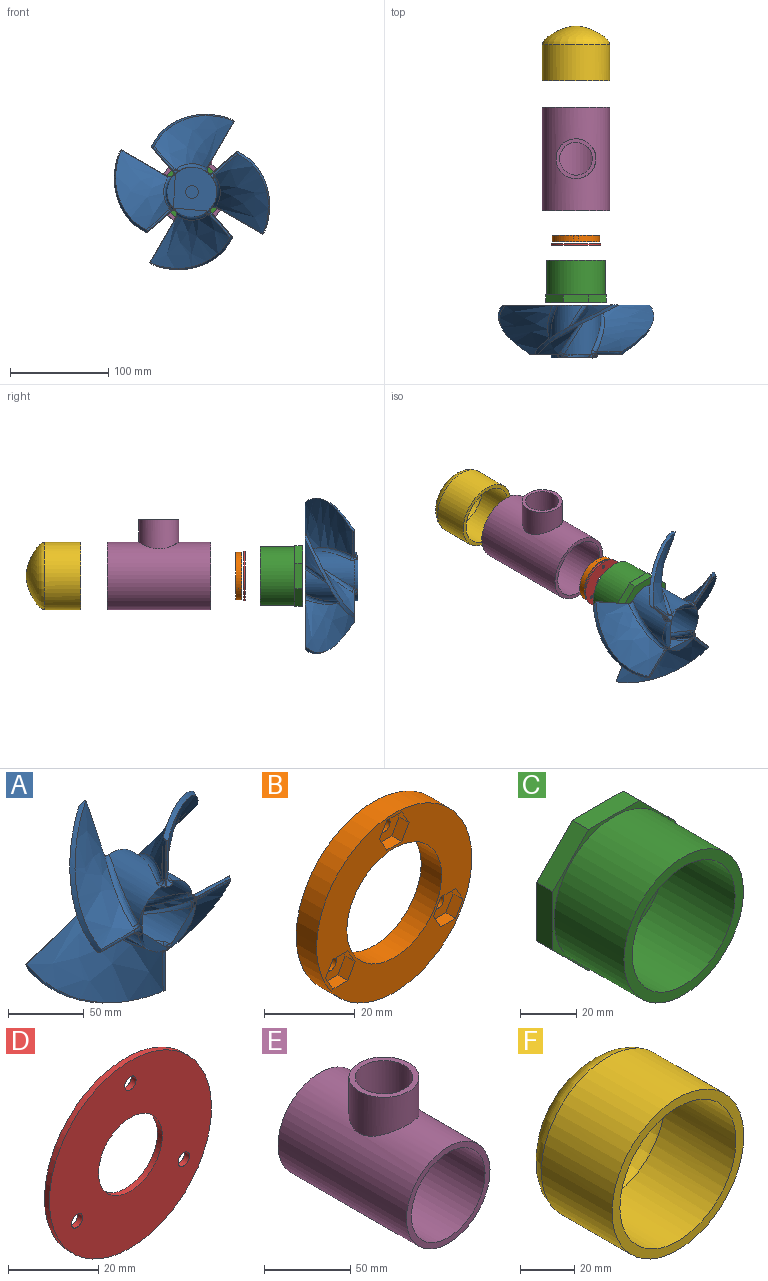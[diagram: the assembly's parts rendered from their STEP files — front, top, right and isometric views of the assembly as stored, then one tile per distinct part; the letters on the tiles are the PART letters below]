
ASSEMBLY  parts=6 mates=5
PART A: 68 faces, bbox 182.4x97.7x182.4 mm
  f0: cylinder r=25.4mm len=50.14mm, axis (0,1,0), area 1388.4mm2, adj f28,f41,f42,f43,f65
  f1: cylinder r=25.4mm len=50.14mm, axis (0,1,0), area 1388.4mm2, adj f28,f48,f49,f50,f65
  f2: cylinder r=25.4mm len=50.14mm, axis (0,1,0), area 1388.4mm2, adj f28,f29,f55,f56,f65
  f3: bspline ~88.12x82.83mm, area 3439.5mm2, adj f8,f34,f60,f65
  f4: plane 32.17x1.13mm, normal (0,-0.85,0.53), area 14.9mm2, adj f7,f8,f32,f60
  f5: bspline ~85.79x85.35mm, area 3695.9mm2, adj f6,f7,f29,f30,f60,f64
  f6: plane 51.13x17.15mm, normal (-0.51,0.85,-0.16), area 35.2mm2, adj f5,f60,f64,f65
  f7: bspline ~31.48x2.18mm, area 62.3mm2, adj f4,f5,f31,f60
  f8: bspline ~68.56x3.02mm, area 87mm2, adj f3,f4,f33,f35,f60
  f9: bspline ~88.12x82.83mm, area 3439.5mm2, adj f14,f41,f59,f65
  f10: plane 32.17x1.13mm, normal (-0.53,-0.85,0), area 14.9mm2, adj f13,f14,f39,f59
  f11: bspline ~85.79x85.35mm, area 3695.9mm2, adj f12,f13,f36,f37,f59,f63
  f12: plane 51.13x17.15mm, normal (0.16,0.85,-0.51), area 35.2mm2, adj f11,f59,f63,f65
  f13: bspline ~31.48x2.18mm, area 62.3mm2, adj f10,f11,f38,f59
  f14: bspline ~68.56x3.02mm, area 87mm2, adj f9,f10,f40,f42,f59
  f15: bspline ~88.12x82.83mm, area 3439.5mm2, adj f20,f48,f58,f65
  f16: plane 32.17x1.13mm, normal (0,-0.85,-0.53), area 14.9mm2, adj f19,f20,f46,f58
  f17: bspline ~85.79x85.35mm, area 3695.9mm2, adj f18,f19,f43,f44,f58,f62
  f18: plane 51.13x17.15mm, normal (0.51,0.85,0.16), area 35.2mm2, adj f17,f58,f62,f65
  f19: bspline ~31.48x2.18mm, area 62.3mm2, adj f16,f17,f45,f58
  f20: bspline ~68.56x3.02mm, area 87mm2, adj f15,f16,f47,f49,f58
  f21: bspline ~88.12x82.83mm, area 3439.5mm2, adj f26,f55,f57,f65
  f22: plane 32.17x1.13mm, normal (0.53,-0.85,0), area 14.9mm2, adj f25,f26,f53,f57
  f23: bspline ~85.79x85.35mm, area 3695.9mm2, adj f24,f25,f50,f51,f57,f61
  f24: plane 51.13x17.15mm, normal (-0.16,0.85,0.51), area 35.2mm2, adj f23,f57,f61,f65
  f25: bspline ~31.48x2.18mm, area 62.3mm2, adj f22,f23,f52,f57
  f26: bspline ~68.56x3.02mm, area 87mm2, adj f21,f22,f54,f56,f57
  f27: cylinder r=25.4mm len=50.14mm, axis (0,1,0), area 1388.4mm2, adj f28,f34,f35,f36,f65
  f28: revolved ~50.8x50.8mm, area 5109.2mm2, adj f0,f1,f2,f27,f29,f30,f31,f32
  f29: bspline ~54.51x27.12mm, area 320.1mm2, adj f2,f5,f28,f30,f64,f65
  f30: bspline ~5.63x4.85mm, area 11.6mm2, adj f5,f28,f29,f31
  f31: bspline ~6.43x4.12mm, area 21.8mm2, adj f7,f28,f30,f32
  f32: bspline ~7.96x6.87mm, area 3.1mm2, adj f4,f28,f31,f33
  f33: bspline ~4.1x3.79mm, area 9.6mm2, adj f8,f28,f32,f35
  f34: bspline ~53.78x31.69mm, area 305.8mm2, adj f3,f27,f35,f65
  f35: bspline ~5.55x3.78mm, area 14.8mm2, adj f8,f27,f28,f33,f34
  f36: bspline ~54.51x27.12mm, area 320.1mm2, adj f11,f27,f28,f37,f63,f65
  f37: bspline ~5.63x4.85mm, area 11.6mm2, adj f11,f28,f36,f38
  f38: bspline ~6.43x4.12mm, area 21.8mm2, adj f13,f28,f37,f39
  f39: bspline ~7.96x6.87mm, area 3.1mm2, adj f10,f28,f38,f40
  f40: bspline ~4.1x3.79mm, area 9.6mm2, adj f14,f28,f39,f42
  f41: bspline ~53.78x31.69mm, area 305.8mm2, adj f0,f9,f42,f65
  f42: bspline ~5.55x3.78mm, area 14.8mm2, adj f0,f14,f28,f40,f41
  f43: bspline ~54.51x27.12mm, area 320.1mm2, adj f0,f17,f28,f44,f62,f65
  f44: bspline ~5.63x4.85mm, area 11.6mm2, adj f17,f28,f43,f45
  f45: bspline ~6.43x4.12mm, area 21.8mm2, adj f19,f28,f44,f46
  f46: bspline ~3.79x3.17mm, area 3.1mm2, adj f16,f28,f45,f47
  f47: bspline ~4.1x3.79mm, area 9.6mm2, adj f20,f28,f46,f49
  f48: bspline ~53.78x31.69mm, area 305.8mm2, adj f1,f15,f49,f65
  f49: bspline ~5.55x3.78mm, area 14.8mm2, adj f1,f20,f28,f47,f48
  f50: bspline ~54.51x27.12mm, area 320.1mm2, adj f1,f23,f28,f51,f61,f65
  f51: bspline ~5.63x4.85mm, area 11.6mm2, adj f23,f28,f50,f52
  f52: bspline ~6.43x4.12mm, area 21.8mm2, adj f25,f28,f51,f53
  f53: bspline ~3.79x3.17mm, area 3.1mm2, adj f22,f28,f52,f54
  f54: bspline ~4.1x3.79mm, area 9.6mm2, adj f26,f28,f53,f56
  f55: bspline ~53.78x31.69mm, area 305.8mm2, adj f2,f21,f56,f65
  f56: bspline ~5.55x3.78mm, area 14.8mm2, adj f2,f26,f28,f54,f55
  f57: revolved ~80.25x66.46mm, area 381.9mm2, adj f21,f22,f23,f24,f25,f26,f65
  f58: revolved ~80.25x66.46mm, area 381.9mm2, adj f15,f16,f17,f18,f19,f20,f65
  f59: revolved ~80.25x66.46mm, area 381.9mm2, adj f9,f10,f11,f12,f13,f14,f65
  f60: revolved ~80.25x66.46mm, area 381.9mm2, adj f3,f4,f5,f6,f7,f8,f65
  f61: bspline ~2.2x1.56mm, area 0.6mm2, adj f23,f24,f50,f65
  f62: bspline ~2.2x1.56mm, area 0.6mm2, adj f17,f18,f43,f65
  f63: bspline ~2.2x1.56mm, area 0.6mm2, adj f11,f12,f36,f65
  f64: bspline ~2.2x1.56mm, area 0.6mm2, adj f5,f6,f29,f65
  f65: plane 161.14x161.14mm, normal (0,1,0), area 3088.6mm2, adj f0,f1,f2,f3,f6,f9,f12,f15
  f66: plane 12.7x12.7mm, normal (0,1,0), area 126.7mm2, adj f67
  f67: cylinder r=6.35mm len=24.74mm, axis (0,1,0), area 986.9mm2, adj f65,f66
PART B: 28 faces, bbox 48.3x6.4x48.3 mm
  f0: plane 48.26x48.26mm, normal (0,-1,0), area 981.1mm2, adj f1,f2,f4,f5,f6,f7,f8,f9
  f1: cylinder r=14.73mm len=29.46mm, axis (0,1,0), area 587.8mm2, adj f0,f3
  f2: cylinder r=24.13mm len=48.26mm, axis (0,1,0), area 962.7mm2, adj f0,f3
  f3: plane 48.26x48.26mm, normal (0,1,0), area 1117.6mm2, adj f1,f2,f25,f26,f27
  f4: plane 4.62x3.05mm, normal (0,0,1), area 14.1mm2, adj f0,f5,f9,f10
  f5: plane 4x3.05mm, normal (-0.87,0,0.5), area 14.1mm2, adj f0,f4,f6,f10
  f6: plane 4x3.05mm, normal (-0.87,0,-0.5), area 14.1mm2, adj f0,f5,f7,f10
  f7: plane 4.62x3.05mm, normal (0,0,-1), area 14.1mm2, adj f0,f6,f8,f10
  f8: plane 4x3.05mm, normal (0.87,0,-0.5), area 14.1mm2, adj f0,f7,f9,f10
  f9: plane 4x3.05mm, normal (0.87,0,0.5), area 14.1mm2, adj f0,f4,f8,f10
  f10: plane 9.24x8mm, normal (0,-1,0), area 45.5mm2, adj f4,f5,f6,f7,f8,f9,f27
  f11: plane 4x3.05mm, normal (0.87,0,-0.5), area 14.1mm2, adj f0,f12,f16,f17
  f12: plane 4x3.05mm, normal (0.87,0,0.5), area 14.1mm2, adj f0,f11,f13,f17
  f13: plane 4.62x3.05mm, normal (0,0,1), area 14.1mm2, adj f0,f12,f14,f17
  f14: plane 4x3.05mm, normal (-0.87,0,0.5), area 14.1mm2, adj f0,f13,f15,f17
  f15: plane 4x3.05mm, normal (-0.87,0,-0.5), area 14.1mm2, adj f0,f14,f16,f17
  f16: plane 4.62x3.05mm, normal (0,0,-1), area 14.1mm2, adj f0,f11,f15,f17
  f17: plane 9.24x8mm, normal (0,-1,0), area 45.5mm2, adj f11,f12,f13,f14,f15,f16,f26
  f18: plane 4.62x3.05mm, normal (0,0,-1), area 14.1mm2, adj f0,f19,f23,f24
  f19: plane 4x3.05mm, normal (0.87,0,-0.5), area 14.1mm2, adj f0,f18,f20,f24
  f20: plane 4x3.05mm, normal (0.87,0,0.5), area 14.1mm2, adj f0,f19,f21,f24
  f21: plane 4.62x3.05mm, normal (0,0,1), area 14.1mm2, adj f0,f20,f22,f24
  f22: plane 4x3.05mm, normal (-0.87,0,0.5), area 14.1mm2, adj f0,f21,f23,f24
  f23: plane 4x3.05mm, normal (-0.87,0,-0.5), area 14.1mm2, adj f0,f18,f22,f24
  f24: plane 9.24x8mm, normal (0,-1,0), area 45.5mm2, adj f18,f19,f20,f21,f22,f23,f25
  f25: cylinder r=1.78mm len=3.56mm, axis (0,-1,0), area 36.9mm2, adj f3,f24
  f26: cylinder r=1.78mm len=3.56mm, axis (0,-1,0), area 36.9mm2, adj f3,f17
  f27: cylinder r=1.78mm len=3.56mm, axis (0,-1,0), area 36.9mm2, adj f3,f10
PART C: 20 faces, bbox 61.5x43.2x61.5 mm
  f0: plane 25.46x8.13mm, normal (0,0,1), area 206.9mm2, adj f1,f7,f8,f9
  f1: plane 18x18mm, normal (-0.71,0,0.71), area 206.9mm2, adj f0,f2,f8,f9
  f2: plane 25.46x8.13mm, normal (-1,0,0), area 206.9mm2, adj f1,f3,f8,f9
  f3: plane 18x18mm, normal (-0.71,0,-0.71), area 206.9mm2, adj f2,f4,f8,f9
  f4: plane 25.46x8.13mm, normal (0,0,-1), area 206.9mm2, adj f3,f5,f8,f9
  f5: plane 18x18mm, normal (0.71,0,-0.71), area 206.9mm2, adj f4,f6,f8,f9
  f6: plane 25.46x8.13mm, normal (1,0,0), area 206.9mm2, adj f5,f7,f8,f9
  f7: plane 18x18mm, normal (0.71,0,0.71), area 206.9mm2, adj f0,f6,f8,f9
  f8: plane 61.47x61.47mm, normal (0,-1,0), area 295.9mm2, adj f0,f1,f2,f3,f4,f5,f6,f7
  f9: plane 61.47x61.47mm, normal (0,1,0), area 2973.6mm2, adj f0,f1,f2,f3,f4,f5,f6,f7
  f10: cylinder r=25.84mm len=51.69mm, axis (0,1,0), area 5691.9mm2, adj f12,f13
  f11: cylinder r=30.04mm len=60.07mm, axis (0,1,0), area 6615mm2, adj f8,f12
  f12: plane 60.07x60.07mm, normal (0,-1,0), area 735.7mm2, adj f10,f11
  f13: plane 51.69x51.69mm, normal (0,-1,0), area 1754.8mm2, adj f10,f14,f17,f18,f19
  f14: cylinder r=9.99mm len=19.99mm, axis (0,-1,0), area 350.9mm2, adj f13,f15
  f15: plane 19.99x19.99mm, normal (0,-1,0), area 187.2mm2, adj f14,f16
  f16: cylinder r=6.35mm len=12.7mm, axis (0,-1,0), area 101.3mm2, adj f9,f15
  f17: cylinder r=1.78mm len=8.13mm, axis (0,-1,0), area 90.8mm2, adj f9,f13
  f18: cylinder r=1.78mm len=8.13mm, axis (0,-1,0), area 90.8mm2, adj f9,f13
  f19: cylinder r=1.78mm len=8.13mm, axis (0,-1,0), area 90.8mm2, adj f9,f13
PART D: 7 faces, bbox 50.8x1.5x50.8 mm
  f0: cylinder r=9.99mm len=19.99mm, axis (0,1,0), area 95.7mm2, adj f2,f3
  f1: cylinder r=25.4mm len=50.8mm, axis (0,1,0), area 243.2mm2, adj f2,f3
  f2: plane 50.8x50.8mm, normal (0,-1,0), area 1683.2mm2, adj f0,f1,f4,f5,f6
  f3: plane 50.8x50.8mm, normal (0,1,0), area 1683.2mm2, adj f0,f1,f4,f5,f6
  f4: cylinder r=1.78mm len=3.56mm, axis (0,-1,0), area 17mm2, adj f2,f3
  f5: cylinder r=1.78mm len=3.56mm, axis (0,-1,0), area 17mm2, adj f2,f3
  f6: cylinder r=1.78mm len=3.56mm, axis (0,-1,0), area 17mm2, adj f2,f3
PART E: 7 faces, bbox 68.6x105.4x91.7 mm
  f0: cylinder r=30.23mm len=105.41mm, axis (0,1,0), area 19103.6mm2, adj f2,f3,f6
  f1: cylinder r=34.29mm len=105.41mm, axis (0,1,0), area 21349.5mm2, adj f2,f3,f5
  f2: plane 68.58x68.58mm, normal (0,-1,0), area 823.7mm2, adj f0,f1
  f3: plane 68.58x68.58mm, normal (0,1,0), area 823.7mm2, adj f0,f1
  f4: plane 40.64x40.64mm, normal (0,0,1), area 421mm2, adj f5,f6
  f5: cylinder r=20.32mm len=40.64mm, axis (0,0,1), area 3365mm2, adj f1,f4
  f6: cylinder r=16.7mm len=33.4mm, axis (0,0,1), area 3109.7mm2, adj f0,f4
PART F: 5 faces, bbox 68.6x55.9x68.6 mm
  f0: cylinder r=30.23mm len=60.45mm, axis (0,1,0), area 6994.6mm2, adj f1,f4
  f1: plane 68.58x68.58mm, normal (0,-1,0), area 823.7mm2, adj f0,f2
  f2: cylinder r=34.29mm len=68.58mm, axis (0,1,0), area 7935mm2, adj f1,f3
  f3: revolved ~68.58x68.58mm, area 4955mm2, adj f2
  f4: revolved ~60.45x60.45mm, area 3603.2mm2, adj f0
PLACE A rot(axis=(0,1,0),47.7deg) t=(0,-88.11,0)mm
PLACE B rot(axis=(0,0,1),180deg) t=(0,4.32,0)mm
PLACE C rot(axis=(0,0,1),180deg) t=(0,-60.83,0)mm fixed
PLACE D t=(0,-0.89,0)mm
PLACE E t=(0,85.6,0)mm
PLACE F t=(0,183.39,0)mm
MATE slider C.f10 <-> D.f1  axis (0,1,0) through (0,-52.7,0)mm
MATE slider E.f0 <-> F.f0  axis (0,1,0) through (0,138.3,0)mm
MATE revolute C.f16 <-> A.f0  axis (0,-1,0) through (0,-60.83,0)mm
MATE slider E.f0 <-> C.f10  axis (0,1,0) through (0,32.89,0)mm
MATE fastened D.f0 <-> B.f1  axis (0,1,0) through (0,-0.89,0)mm
